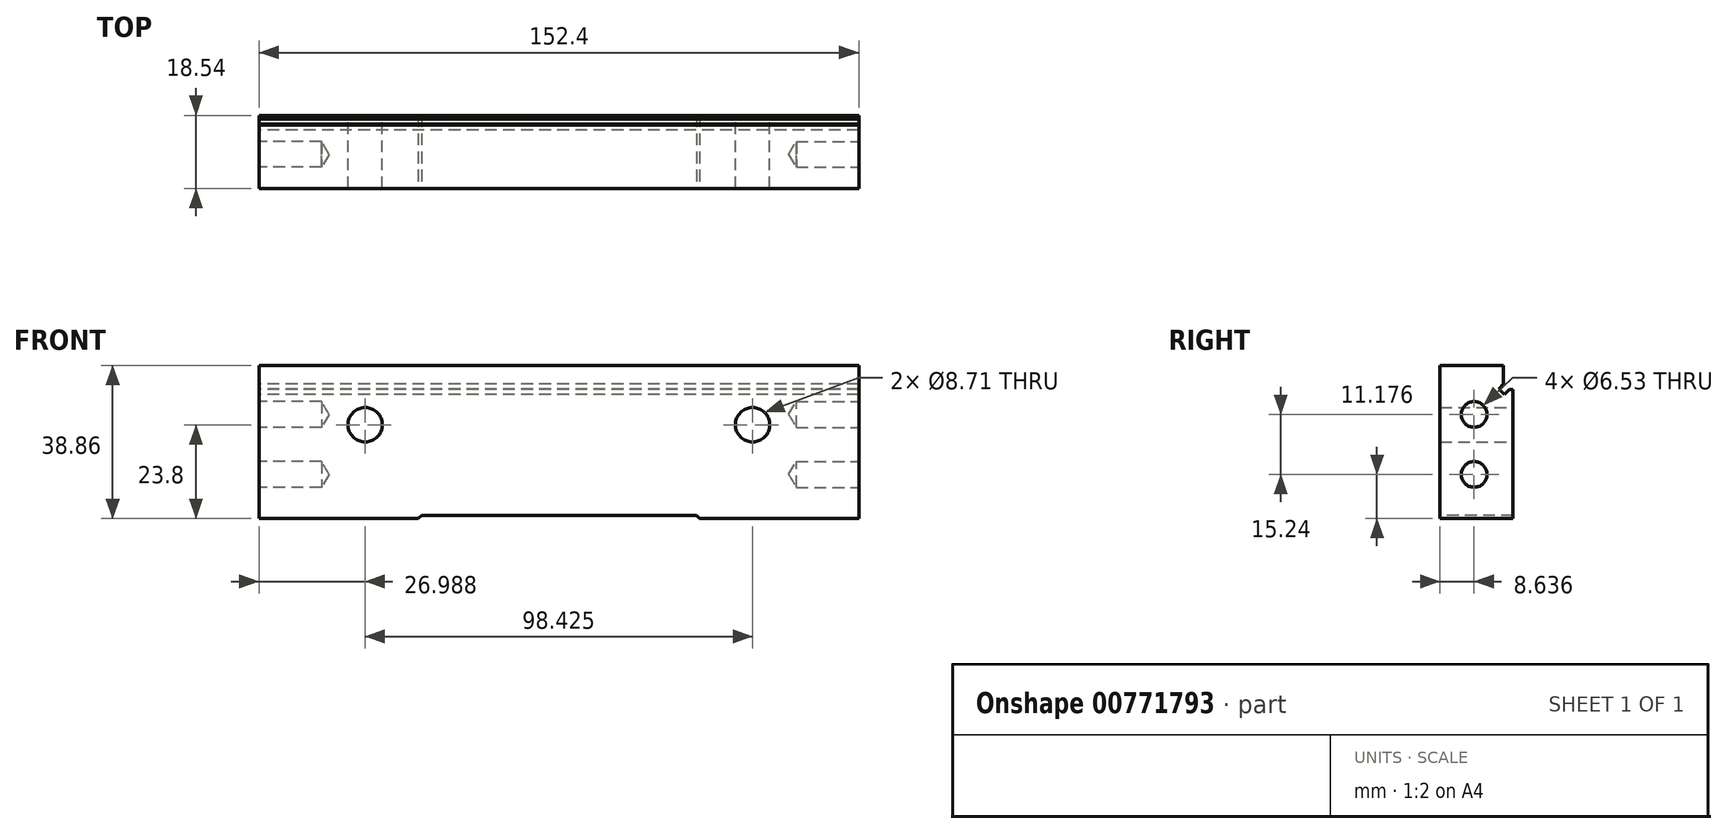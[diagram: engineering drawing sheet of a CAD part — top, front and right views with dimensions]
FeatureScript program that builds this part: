
annotation { "Feature Type Name" : "Feature", "Feature Type Description" : "" }
export const myFeature = defineFeature(function(context is Context, id is Id, definition is map)
    precondition{}
    {
        {
            var Q0;
            Q0=qCreatedBy(makeId("Right.planeOp"),FACE);
            var sketch = newSketch(context, id + "F0", { "sketchPlane" : qUnion([Q0])});
            skLineSegment(sketch, "E0", {"start": v(0, 0) * mm, "end": v(0, 38.86) * mm});
            skLineSegment(sketch, "E1", {"start": v(0, 38.86) * mm, "end": v(16.13, 38.86) * mm});
            skLineSegment(sketch, "E2", {"start": v(16.13, 38.86) * mm, "end": v(16.13, 34.2) * mm});
            skLineSegment(sketch, "E3", {"start": v(17.57, 32.77) * mm, "end": v(18.54, 32.77) * mm});
            skLineSegment(sketch, "E4", {"start": v(18.54, 32.77) * mm, "end": v(18.54, 0) * mm});
            skLineSegment(sketch, "E5", {"start": v(18.54, 0) * mm, "end": v(0, 0) * mm});
            skLineSegment(sketch, "E6", {"start": v(16.13, 34.2) * mm, "end": v(14.87, 32.95) * mm});
            skLineSegment(sketch, "E7", {"start": v(14.87, 32.95) * mm, "end": v(16.3, 31.5) * mm});
            skLineSegment(sketch, "E8", {"start": v(16.3, 31.5) * mm, "end": v(17.57, 32.77) * mm});
            skPoint(sketch, "E9.orphan", {"position": v(16.13, 32.77) * mm});
            skSolve(sketch);
        }
        {
            var Q0;
            Q0=qSketchRegion(id+"F0",true);
            extrude(context, id + "F1", {"entities" : qUnion([Q0]), "depth" : 76.2 * mm, "offsetDistance" : 25.4 * mm, "hasSecondDirection" : true, "secondDirectionOppositeDirection" : true, "secondDirectionDepth" : 76.2 * mm});
        }
        {
            var Q0;
            Q0=makeQuery(id+"F1.opExtrude","CAP_FACE",FACE,{"disambiguationData":[OSD([sQuery(id+"F0.wireOp",EDGE,"E0"),sQuery(id+"F0.wireOp",EDGE,"E1"),sQuery(id+"F0.wireOp",EDGE,"E2"),sQuery(id+"F0.wireOp",EDGE,"E3"),sQuery(id+"F0.wireOp",EDGE,"E4"),sQuery(id+"F0.wireOp",EDGE,"E5"),sQuery(id+"F0.wireOp",EDGE,"E6"),sQuery(id+"F0.wireOp",EDGE,"E7"),sQuery(id+"F0.wireOp",EDGE,"E8")])],"isStart":false});
            var sketch = newSketch(context, id + "F2", { "sketchPlane" : qUnion([Q0])});
            skCircle(sketch, "E10", {"center": v(8.64, 26.42) * mm, "radius": 3.97 * mm});
            skCircle(sketch, "E11", {"center": v(8.64, 11.18) * mm, "radius": 3.97 * mm});
            skSolve(sketch);
        }
        {
            var Q0;
            Q0=sQuery(id+"F2.wireOp",VERTEX,"E11.center");
            var Q1;
            Q1=sQuery(id+"F2.wireOp",VERTEX,"E10.center");
            var Q2;
            Q2=makeQuery(id+"F1.opExtrude","SWEPT_BODY",BODY,{"disambiguationData":[OSD([sQuery(id+"F0.wireOp",EDGE,"E0"),sQuery(id+"F0.wireOp",EDGE,"E1"),sQuery(id+"F0.wireOp",EDGE,"E2"),sQuery(id+"F0.wireOp",EDGE,"E3"),sQuery(id+"F0.wireOp",EDGE,"E4"),sQuery(id+"F0.wireOp",EDGE,"E5"),sQuery(id+"F0.wireOp",EDGE,"E6"),sQuery(id+"F0.wireOp",EDGE,"E7"),sQuery(id+"F0.wireOp",EDGE,"E8")])]});
            hole(context, id + "F3", {"style" : HoleStyle.SIMPLE, "endStyle" : HoleEndStyle.BLIND, "standardTappedOrClearance" : lookupTablePath({ "standard" : "ANSI", "engagement" : "75%", "pitch" : "18 tpi", "size" : "5/16", "type" : "Tapped" }), "standardBlindInLast" : lookupTablePath({ "standard" : "ANSI", "engagement" : "75%", "pitch" : "18 tpi", "size" : "5/16", "type" : "Tapped" }), "holeDiameter" : 6.53 * mm, "majorDiameter" : 7.94 * mm, "showTappedDepth" : true, "holeDepth" : 15.88 * mm, "isTappedThrough" : true, "tappedDepth" : 11.64 * mm, "tapClearance" : 3, "locations" : qUnion([Q0, Q1]), "scope" : qUnion([Q2])});
        }
        {
            var Q0;
            Q0=makeQuery(id+"F1.opExtrude","CAP_FACE",FACE,{"disambiguationData":[OSD([sQuery(id+"F0.wireOp",EDGE,"E0"),sQuery(id+"F0.wireOp",EDGE,"E1"),sQuery(id+"F0.wireOp",EDGE,"E2"),sQuery(id+"F0.wireOp",EDGE,"E3"),sQuery(id+"F0.wireOp",EDGE,"E4"),sQuery(id+"F0.wireOp",EDGE,"E5"),sQuery(id+"F0.wireOp",EDGE,"E6"),sQuery(id+"F0.wireOp",EDGE,"E7"),sQuery(id+"F0.wireOp",EDGE,"E8")])],"isStart":true});
            var sketch = newSketch(context, id + "F4", { "sketchPlane" : qUnion([Q0])});
            skCircle(sketch, "E12.0", {"center": v(-8.64, 11.18) * mm, "radius": 3.26 * mm});
            skCircle(sketch, "E13.0", {"center": v(-8.64, 26.42) * mm, "radius": 3.26 * mm});
            skSolve(sketch);
        }
        {
            var Q0;
            Q0=sQuery(id+"F4.wireOp",VERTEX,"E13.0.center");
            var Q1;
            Q1=sQuery(id+"F4.wireOp",VERTEX,"E12.0.center");
            var Q2;
            Q2=makeQuery(id+"F1.opExtrude","SWEPT_BODY",BODY,{"disambiguationData":[OSD([sQuery(id+"F0.wireOp",EDGE,"E0"),sQuery(id+"F0.wireOp",EDGE,"E1"),sQuery(id+"F0.wireOp",EDGE,"E2"),sQuery(id+"F0.wireOp",EDGE,"E3"),sQuery(id+"F0.wireOp",EDGE,"E4"),sQuery(id+"F0.wireOp",EDGE,"E5"),sQuery(id+"F0.wireOp",EDGE,"E6"),sQuery(id+"F0.wireOp",EDGE,"E7"),sQuery(id+"F0.wireOp",EDGE,"E8")])]});
            hole(context, id + "F5", {"style" : HoleStyle.SIMPLE, "endStyle" : HoleEndStyle.BLIND, "standardTappedOrClearance" : lookupTablePath({ "standard" : "ANSI", "engagement" : "75%", "pitch" : "18 tpi", "size" : "5/16", "type" : "Tapped" }), "standardBlindInLast" : lookupTablePath({ "standard" : "ANSI", "engagement" : "75%", "pitch" : "18 tpi", "size" : "5/16", "type" : "Tapped" }), "holeDiameter" : 6.53 * mm, "majorDiameter" : 7.94 * mm, "showTappedDepth" : true, "holeDepth" : 15.88 * mm, "isTappedThrough" : true, "tappedDepth" : 11.64 * mm, "tapClearance" : 3, "locations" : qUnion([Q0, Q1]), "scope" : qUnion([Q2])});
        }
        {
            var Q0;
            Q0=makeQuery(id+"F1.opExtrude","SWEPT_FACE",FACE,{"disambiguationData":[OSD([sQuery(id+"F0.wireOp",EDGE,"E0")])]});
            var sketch = newSketch(context, id + "F6", { "sketchPlane" : qUnion([Q0])});
            skLineSegment(sketch, "E14", {"start": v(-35.73, 0) * mm, "end": v(-34.93, 0.8) * mm});
            skLineSegment(sketch, "E15", {"start": v(-34.93, 0.8) * mm, "end": v(34.93, 0.8) * mm});
            skLineSegment(sketch, "E16", {"start": v(34.93, 0.8) * mm, "end": v(35.73, 0) * mm});
            skLineSegment(sketch, "E17", {"start": v(-35.73, 0) * mm, "end": v(35.73, 0) * mm});
            skSolve(sketch);
        }
        {
            var Q0;
            Q0=makeQuery(id+"F6.imprint","IMPRINT",FACE,{"disambiguationData":[TD([[makeQuery(id+"F6.imprint","IMPRINT",EDGE,{"derivedFrom":sQuery(id+"F6.wireOp",EDGE,"E14")}),-1.0]])]});
            extrude(context, id + "F7", {"entities" : qUnion([Q0]), "operationType" : NewBodyOperationType.REMOVE, "endBound" : BoundingType.THROUGH_ALL, "oppositeDirection" : true, "depth" : 25.4 * mm, "offsetDistance" : 25.4 * mm});
        }
        {
            var Q0;
            Q0=makeQuery(id+"F1.opExtrude","SWEPT_FACE",FACE,{"disambiguationData":[OSD([sQuery(id+"F0.wireOp",EDGE,"E4")])]});
            var sketch = newSketch(context, id + "F8", { "sketchPlane" : qUnion([Q0])});
            skCircle(sketch, "E18", {"center": v(-49.21, 23.8) * mm, "radius": 4.36 * mm});
            skCircle(sketch, "E19", {"center": v(49.21, 23.8) * mm, "radius": 4.36 * mm});
            skSolve(sketch);
        }
        {
            var Q0;
            Q0=qSketchRegion(id+"F8",true);
            extrude(context, id + "F9", {"entities" : qUnion([Q0]), "operationType" : NewBodyOperationType.REMOVE, "endBound" : BoundingType.THROUGH_ALL, "oppositeDirection" : true, "depth" : 25.4 * mm, "offsetDistance" : 25.4 * mm});
        }
    });
